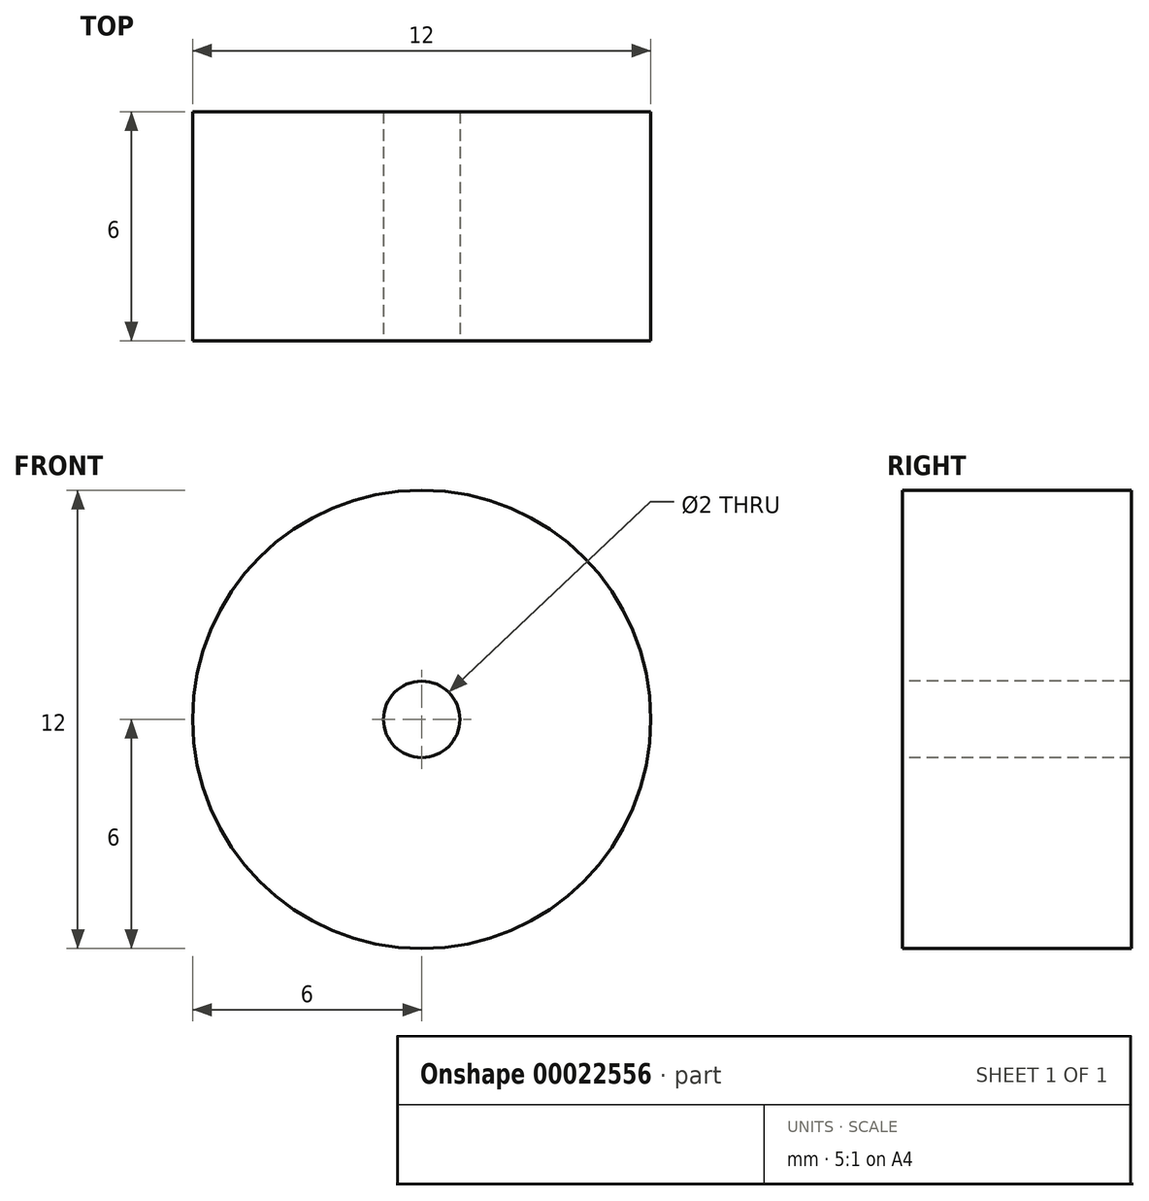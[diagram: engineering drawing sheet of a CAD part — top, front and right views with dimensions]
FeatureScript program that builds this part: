
annotation { "Feature Type Name" : "Feature", "Feature Type Description" : "" }
export const myFeature = defineFeature(function(context is Context, id is Id, definition is map)
    precondition{}
    {
        {
            var Q0;
            Q0=qCreatedBy(makeId("Front.planeOp"),FACE);
            var sketch = newSketch(context, id + "F0", { "sketchPlane" : qUnion([Q0])});
            skCircle(sketch, "E0", {"center": v(0, 0) * mm, "radius": 6 * mm});
            skSolve(sketch);
        }
        {
            var Q0;
            Q0=makeQuery(id+"F0.imprint","IMPRINT",FACE,{"disambiguationData":[TD([[makeQuery(id+"F0.imprint","IMPRINT",EDGE,{"derivedFrom":sQuery(id+"F0.wireOp",EDGE,"E0")}),1.0]])]});
            extrude(context, id + "F1", {"entities" : qUnion([Q0]), "depth" : 6 * mm});
        }
        {
            var Q0;
            Q0=makeQuery(id+"F1.opExtrude","CAP_FACE",FACE,{"disambiguationData":[OSD([sQuery(id+"F0.wireOp",EDGE,"E0")])],"isStart":false});
            var sketch = newSketch(context, id + "F2", { "sketchPlane" : qUnion([Q0])});
            skCircle(sketch, "E1", {"center": v(0, 0) * mm, "radius": 1 * mm});
            skSolve(sketch);
        }
        {
            var Q0;
            Q0=makeQuery(id+"F2.imprint","IMPRINT",FACE,{"disambiguationData":[TD([[makeQuery(id+"F2.imprint","IMPRINT",EDGE,{"derivedFrom":sQuery(id+"F2.wireOp",EDGE,"E1")}),1.0]])]});
            extrude(context, id + "F3", {"entities" : qUnion([Q0]), "operationType" : NewBodyOperationType.REMOVE, "endBound" : BoundingType.THROUGH_ALL, "oppositeDirection" : true, "depth" : 25.4 * mm});
        }
    });
